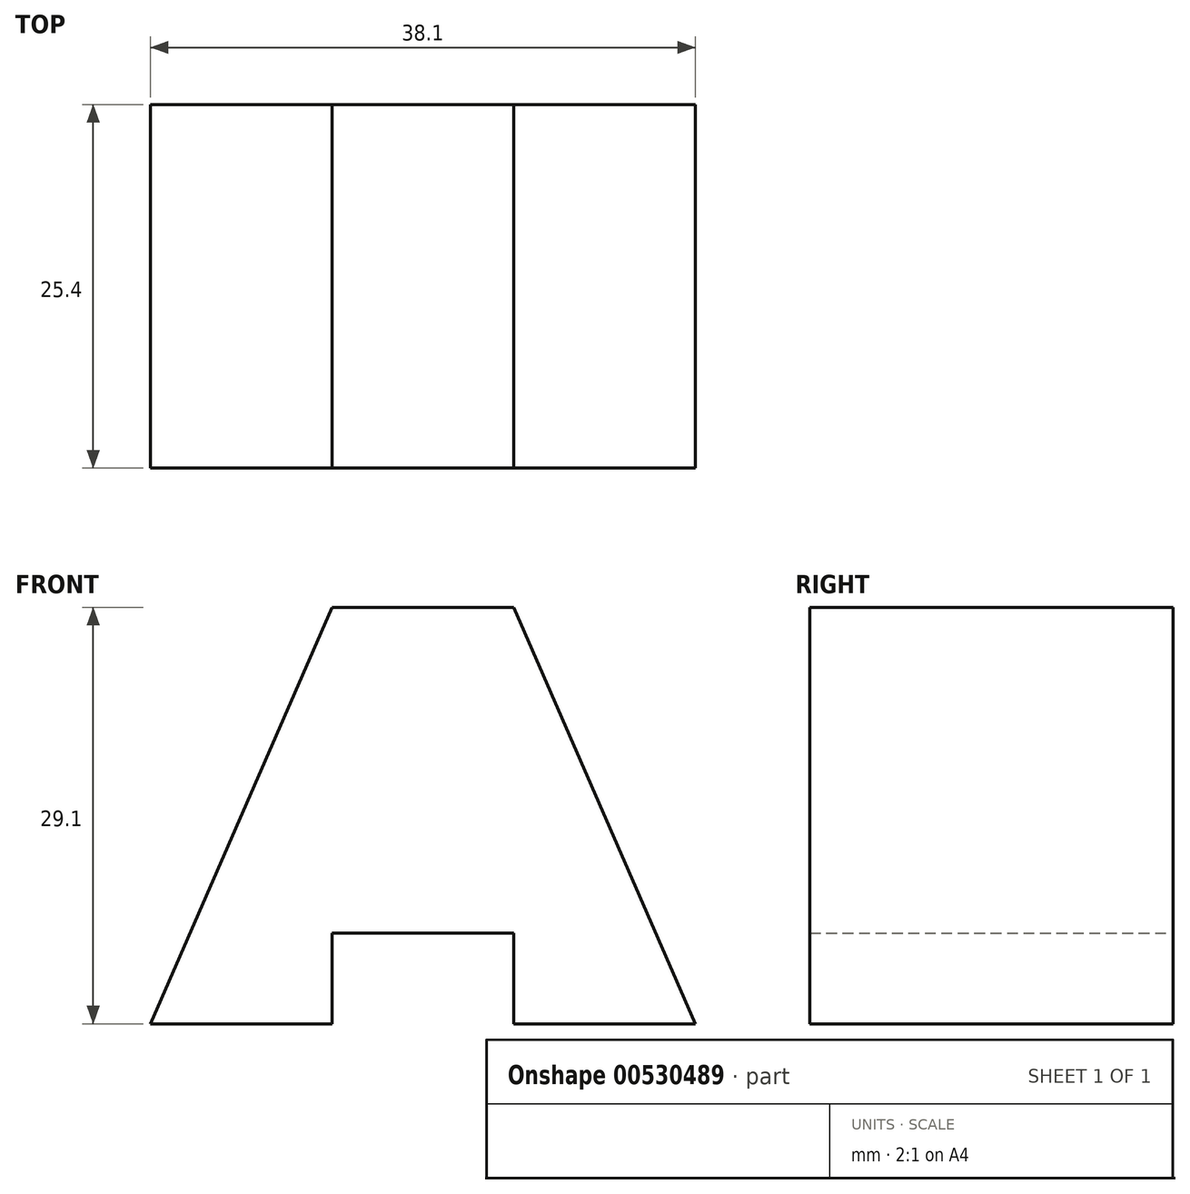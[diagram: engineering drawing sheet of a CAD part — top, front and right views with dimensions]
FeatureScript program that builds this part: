
annotation { "Feature Type Name" : "Feature", "Feature Type Description" : "" }
export const myFeature = defineFeature(function(context is Context, id is Id, definition is map)
    precondition{}
    {
        {
            var Q0;
            Q0=qCreatedBy(makeId("Front.planeOp"),FACE);
            var sketch = newSketch(context, id + "F0", { "sketchPlane" : qUnion([Q0])});
            skLineSegment(sketch, "E0", {"start": v(-69.85, 0) * mm, "end": v(-57.15, 0) * mm});
            skLineSegment(sketch, "E1", {"start": v(-57.15, 0) * mm, "end": v(-57.15, 6.35) * mm});
            skLineSegment(sketch, "E2", {"start": v(-57.15, 6.35) * mm, "end": v(-44.45, 6.35) * mm});
            skLineSegment(sketch, "E3", {"start": v(-44.45, 6.35) * mm, "end": v(-44.45, 0) * mm});
            skLineSegment(sketch, "E4", {"start": v(-44.45, 0) * mm, "end": v(-31.75, 0) * mm});
            skLineSegment(sketch, "E5", {"start": v(-31.75, 0) * mm, "end": v(-44.45, 29.1) * mm});
            skLineSegment(sketch, "E6", {"start": v(-44.45, 29.1) * mm, "end": v(-57.15, 29.1) * mm});
            skLineSegment(sketch, "E7", {"start": v(-57.15, 29.1) * mm, "end": v(-69.85, 0) * mm});
            skSolve(sketch);
        }
        {
            var Q0;
            Q0 = qSketchRegion(id + "F0", true);
            extrude(context, id + "F1", {"entities" : qUnion([Q0]), "depth" : 25.4 * mm, "offsetDistance" : 25.4 * mm});
        }
    });
